# Revit family: PUZ-ZM35VKA2(-ET,ER)
name_source: partatom
category: Mechanical Equipment
revit_build: Autodesk Revit 2018 (Build: 20181015_0930(x64)
units: mm (PartAtom-declared; Revit-internal decimal feet)

## family parameters
Always vertical = Yes
Cut with Voids When Loaded = No
OmniClass Number = 23.75.00.00
OmniClass Title = Climate Control (HVAC)
Part Type = Normal
Room Calculation Point = No
Round Connector Dimension = Use Diameter
Shared = No
Work Plane-Based = No

## types (1)
- PUZ-ZM35VKA2(-ET,ER)
    Compressor = Hermetic
    Compressor Model = SVB140FFSM
    Compressor Motor Output (kW) = 1.0
    Compressor Protection devices = HP switch, Comp.surface thermistor
    Compressor Starter type = Inverter
    Connection method  Indoor side = Flared
    Connection method Outdoor side = Flared
    Cooling Sound pressure level (dB) = 44
    Crankcase heater (kW) = -
    Defrost method = Reverse cycle
    Depth (in) = 11-13/16 + 25/32
    Depth (mm)_ = 300+20
    Description = Outdoor unit
    Equip_No. = 0
    External Finish = Munsell 3Y 7.8/1.1
    Fan Airflow (m3/min) (CFM) = 45 (1590)
    Fan Motor Output (kW) = 0.046
    Fan No. = 1
    Fan drive = Propeller fan
    Heat exchanger = Plate fin coil
    Heating Sound pressure level (dB) = 46
    Height (in) = 24-13/16
    Height (mm)_ = 630
    Hertz = 50 Hz
    Manufacturer = Mitsubishi Electric Corporation
    Maxmum current (A) = 13 A
    Model = PUZ-ZM35VKA2(-ET,ER)
    Phase = 1
    Refrigerant Oil (Model) = FW68S
    Refrigerant Oil Charged (L) = 0.35
    Refrigerant Piping Height difference Between the indoor and outdoor unit(m) = Maximum 30
    Refrigerant Piping length Between the indoor and outdoor unit(m) = Maximum 50
    Refrigerant charged (kg) = 2.0
    Refrigerant charged (lbS) = 4.4
    Refrigerant control = Linear expansion valve
    Refrigerant piping :Pipe size O.D gas (in) = 1/2
    Refrigerant piping :Pipe size O.D gas (mm) = 12.7 mm  [stored 0.0416667 ft]
    Refrigerant piping :Pipe size O.D liquid (in) = 1/4
    Refrigerant piping :Pipe size O.D liquid (mm) = 6.35 mm  [stored 0.0208333 ft]
    Refrigerant type = R32
    SerialNumber = 0
    Space View = Yes
    Subcategory = HVAC
    TagNumber = 0
    URL = http://www.mitsubishielectric.com
    Voltage = 230 V
    Weight (kg) = 46
    Weight (lbs) = 101
    Width (in) = 31-13/16
    Width (mm)_ = 809

note: [stored X ft] marks values corroborated as IEEE doubles in the binary element streams (Revit-internal decimal feet)

## geometry (parser evidence)
native form markers: Blend x34, Sweep x2
no freeform markers — native parametric forms only
